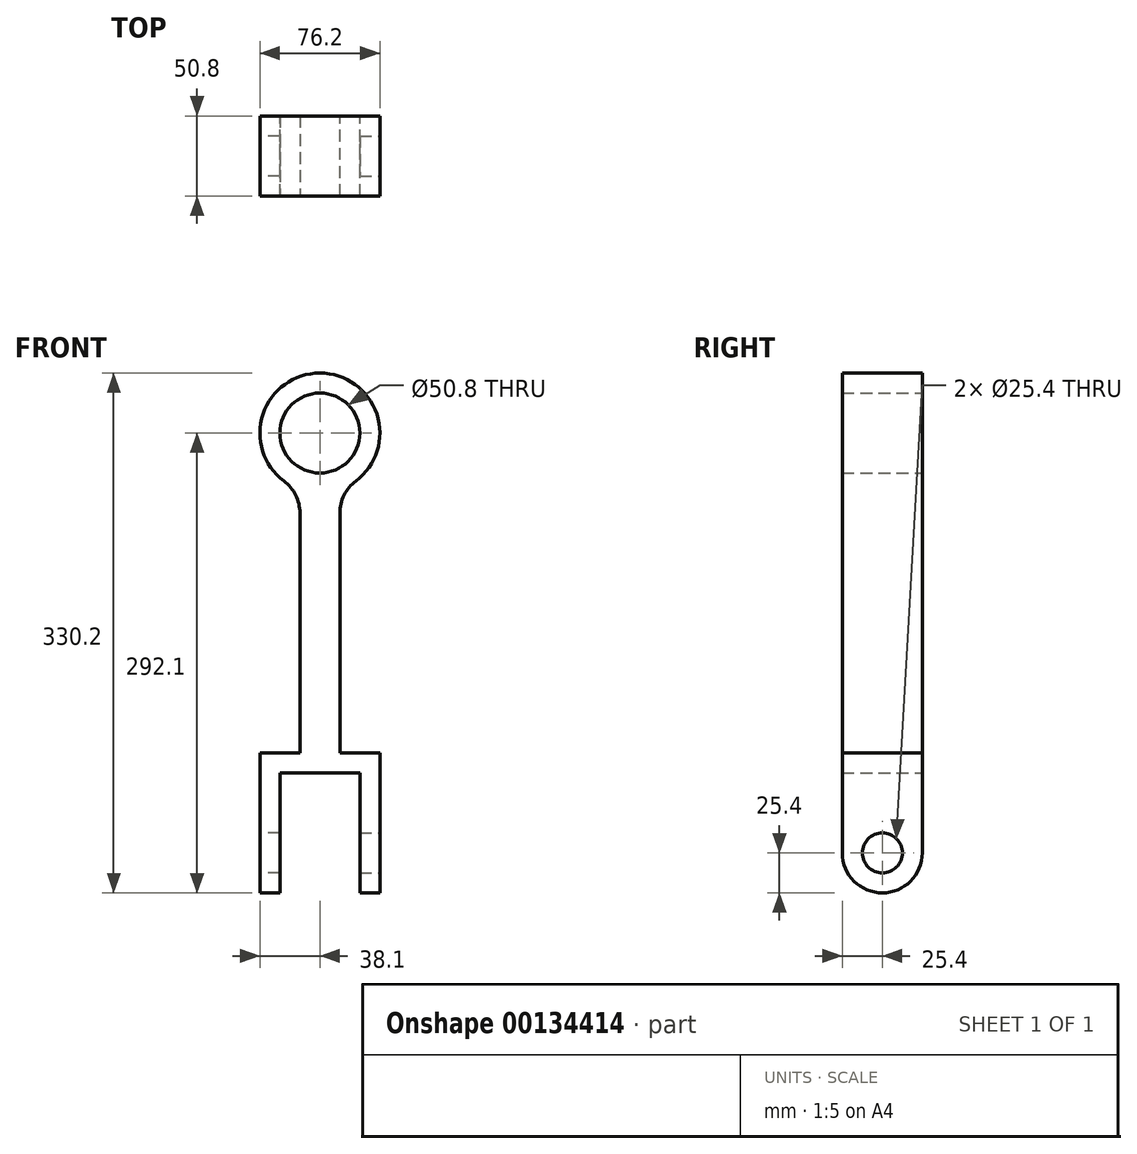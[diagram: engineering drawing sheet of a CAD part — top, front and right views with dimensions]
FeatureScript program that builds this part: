
annotation { "Feature Type Name" : "Feature", "Feature Type Description" : "" }
export const myFeature = defineFeature(function(context is Context, id is Id, definition is map)
    precondition{}
    {
        {
            var Q0;
            Q0=qCreatedBy(makeId("Front.planeOp"),FACE);
            var sketch = newSketch(context, id + "F0", { "sketchPlane" : qUnion([Q0])});
            skCircle(sketch, "E0", {"center": v(0, 0) * mm, "radius": 38.1 * mm});
            skCircle(sketch, "E1", {"center": v(0, 0) * mm, "radius": 25.4 * mm});
            skLineSegment(sketch, "E2", {"start": v(-12.7, -35.92) * mm, "end": v(-12.7, -203.2) * mm});
            skLineSegment(sketch, "E3", {"start": v(-12.7, -203.2) * mm, "end": v(-38.1, -203.2) * mm});
            skLineSegment(sketch, "E4", {"start": v(-38.1, -203.2) * mm, "end": v(-38.1, -292.1) * mm});
            skLineSegment(sketch, "E5", {"start": v(-38.1, -292.1) * mm, "end": v(-25.4, -292.1) * mm});
            skLineSegment(sketch, "E6", {"start": v(38.1, -292.1) * mm, "end": v(38.1, -203.2) * mm});
            skLineSegment(sketch, "E7", {"start": v(38.1, -203.2) * mm, "end": v(12.7, -203.2) * mm});
            skLineSegment(sketch, "E8", {"start": v(12.7, -203.2) * mm, "end": v(12.7, -35.92) * mm});
            skLineSegment(sketch, "E9", {"start": v(-25.4, -292.1) * mm, "end": v(-25.4, -215.9) * mm});
            skLineSegment(sketch, "E10", {"start": v(-25.4, -215.9) * mm, "end": v(25.4, -215.9) * mm});
            skLineSegment(sketch, "E11", {"start": v(25.4, -215.9) * mm, "end": v(25.4, -292.1) * mm});
            skLineSegment(sketch, "E12", {"start": v(25.4, -292.1) * mm, "end": v(38.1, -292.1) * mm});
            skLineSegment(sketch, "E13", {"start": v(0, 0) * mm, "end": v(0, -203.2) * mm, "construction": true});
            skSolve(sketch);
        }
        {
            var Q0;
            Q0 = qSketchRegion(id + "F0", true);
            extrude(context, id + "F1", {"entities" : qUnion([Q0]), "endBound" : BoundingType.SYMMETRIC, "depth" : 50.8 * mm});
        }
        {
            var Q0;
            Q0=makeQuery(id+"F1.opExtrude","SWEPT_EDGE",EDGE,{"disambiguationData":[OSD([sQuery(id+"F0.wireOp",EDGE,"E0"),sQuery(id+"F0.wireOp",EDGE,"E8")])]});
            var Q1;
            Q1=makeQuery(id+"F1.opExtrude","SWEPT_EDGE",EDGE,{"disambiguationData":[OSD([sQuery(id+"F0.wireOp",EDGE,"E0"),sQuery(id+"F0.wireOp",EDGE,"E2")])]});
            var Q2;
            Q2=makeQuery(id+"F1.opExtrude","CAP_EDGE",EDGE,{"disambiguationData":[OSD([sQuery(id+"F0.wireOp",EDGE,"E5")])],"isStart":false});
            var Q3;
            Q3=makeQuery(id+"F1.opExtrude","CAP_EDGE",EDGE,{"disambiguationData":[OSD([sQuery(id+"F0.wireOp",EDGE,"E5")])],"isStart":true});
            var Q4;
            Q4=makeQuery(id+"F1.opExtrude","CAP_EDGE",EDGE,{"disambiguationData":[OSD([sQuery(id+"F0.wireOp",EDGE,"E12")])],"isStart":false});
            var Q5;
            Q5=makeQuery(id+"F1.opExtrude","CAP_EDGE",EDGE,{"disambiguationData":[OSD([sQuery(id+"F0.wireOp",EDGE,"E12")])],"isStart":true});
            fillet(context, id + "F2", {"entities" : qUnion([Q0, Q1, Q2, Q3, Q4, Q5]), "radius" : 25.4 * mm, "tangentPropagation" : true, "allowEdgeOverflow" : false});
        }
        {
            var Q0;
            Q0=makeQuery(id+"F1.opExtrude","SWEPT_FACE",FACE,{"disambiguationData":[OSD([sQuery(id+"F0.wireOp",EDGE,"E4")])]});
            var sketch = newSketch(context, id + "F3", { "sketchPlane" : qUnion([Q0])});
            skCircle(sketch, "E14", {"center": v(0, -266.7) * mm, "radius": 12.7 * mm});
            skPoint(sketch, "E14.centerSnap0", {"position": v(0, -203.2) * mm});
            skSolve(sketch);
        }
        {
            var Q0;
            Q0 = qSketchRegion(id + "F3", true);
            extrude(context, id + "F4", {"entities" : qUnion([Q0]), "operationType" : NewBodyOperationType.REMOVE, "endBound" : BoundingType.UP_TO_NEXT, "oppositeDirection" : true, "depth" : 25.4 * mm});
        }
        {
            var Q0;
            Q0=makeQuery(id+"F1.opExtrude","SWEPT_FACE",FACE,{"disambiguationData":[OSD([sQuery(id+"F0.wireOp",EDGE,"E6")])]});
            var sketch = newSketch(context, id + "F5", { "sketchPlane" : qUnion([Q0])});
            skCircle(sketch, "E15", {"center": v(0, -266.7) * mm, "radius": 12.7 * mm});
            skSolve(sketch);
        }
        {
            var Q0;
            Q0 = qSketchRegion(id + "F5", true);
            extrude(context, id + "F6", {"entities" : qUnion([Q0]), "operationType" : NewBodyOperationType.REMOVE, "endBound" : BoundingType.UP_TO_NEXT, "oppositeDirection" : true, "depth" : 25.4 * mm});
        }
    });
